# Revit family: BasinMixer-Vitra-OriginSeries-A42583
name_source: partatom
category: Plumbing Fixtures
units: mm (PartAtom-declared; Revit-internal decimal feet)

## family parameters
Cut with Voids When Loaded = No
Host = Face
OmniClass Number = 23.45.55.17
OmniClass Title = Mixing Faucets
Part Type = Normal
Room Calculation Point = No
Round Connector Dimension = Use Diameter
Shared = Yes

## types (1)
- BasinMixer-Vitra-OriginSeries(Chrome)-A42583
    Article No. (default) = A42583
    BIMobject category = Taps & Mixers
    CW Connection = Yes
    CWFU = 0
    Coating Material = Vitra-Chrome
    Color = Chrome
    Connection Diameter (mm) = 10 mm  [stored 0.0328084 ft]
    Cost = 0 $
    Default Elevation = 850 mm  [stored 2.78871 ft]
    Depth(mm) = 169 mm
    Description = To clean your product use a soft cloth soaked in alcohol or soap. Never use. acid or hydrochloric acid used to clean closed and floor and never use cleaning salt used to clean basin and sink.
    Design country = Turkey
    HW Connection = Yes
    HWFU = 0
    Height(mm) = 135 mm
    Hot Water Supply (max.) = 80 °C
    Hot Water temperature, factory set to = 38 °C
    IFC Classification = Sanitary Terminal
    Main Material = Brass
    Manufacturer = Vitra
    Manufacturer name = Vitra
    Masterformat 2014 Code = 22 40 00
    Masterformat 2014 Description = Plumbing Fixtures
    Min. flow pressure of = 0.5 bar
    Model = A42583
    MountingType = Counter Top
    NBS Referans Code = 45-35-70/371
    NBS Referans Description = Water supply fittings for wash basins and troughs
    Nominal height = 0.000
    Nominal width = 0.000
    Number Of Connections = 2 mm  [stored 0.00656168 ft]
    OmniClass Code = 23.45.55.17
    OmniClass Description = Mixing Faucets
    Product Properties = Extra Water Saving, Green Building Certification, Energy Saving, Easy İnstallation
    Product SKU = A42583
    Product Type = Basin Mixer
    Product certification = https://vitraglobal.com
    Product data url = https://www.bimobject.com
    Product family = Origin
    Product group = Origin Basin Mixer
    Product url = https://www.vitra.com.tr
    Range of Hot Water Supply = 5 - 65 °C
    Range of flow pressure = 1 - 5 bar
    Technical description = https://www.vitra.com.tr
    Test Pressure = 16 bar
    UNSPSC Code = 301815
    URL = https://vitraglobal.com
    Uniclass 1.4 Code = L725111
    Uniclass 1.4 Description = Mixer taps
    Uniclass 2.0 Code = Pr_40_30_96_98
    Uniclass 2.0 Description = Washbasin Tap
    Uniclass 2015 Code = Pr_40_20_87_98
    Uniclass 2015 Name = Washbasin Tap
    Uniformat II Code = 22 40 00
    Uniformat II Description = Plumbing Fixture
    WFU = 0
    Warranty Period (Year) = 10 Years
    Weight Net (kg) = 2.052
    Width(mm) = 419 mm
    Youtube = https://www.youtube.com

note: [stored X ft] marks values corroborated as IEEE doubles in the binary element streams (Revit-internal decimal feet)

## geometry (parser evidence)
native form markers: Sweep x2
no freeform markers — native parametric forms only
